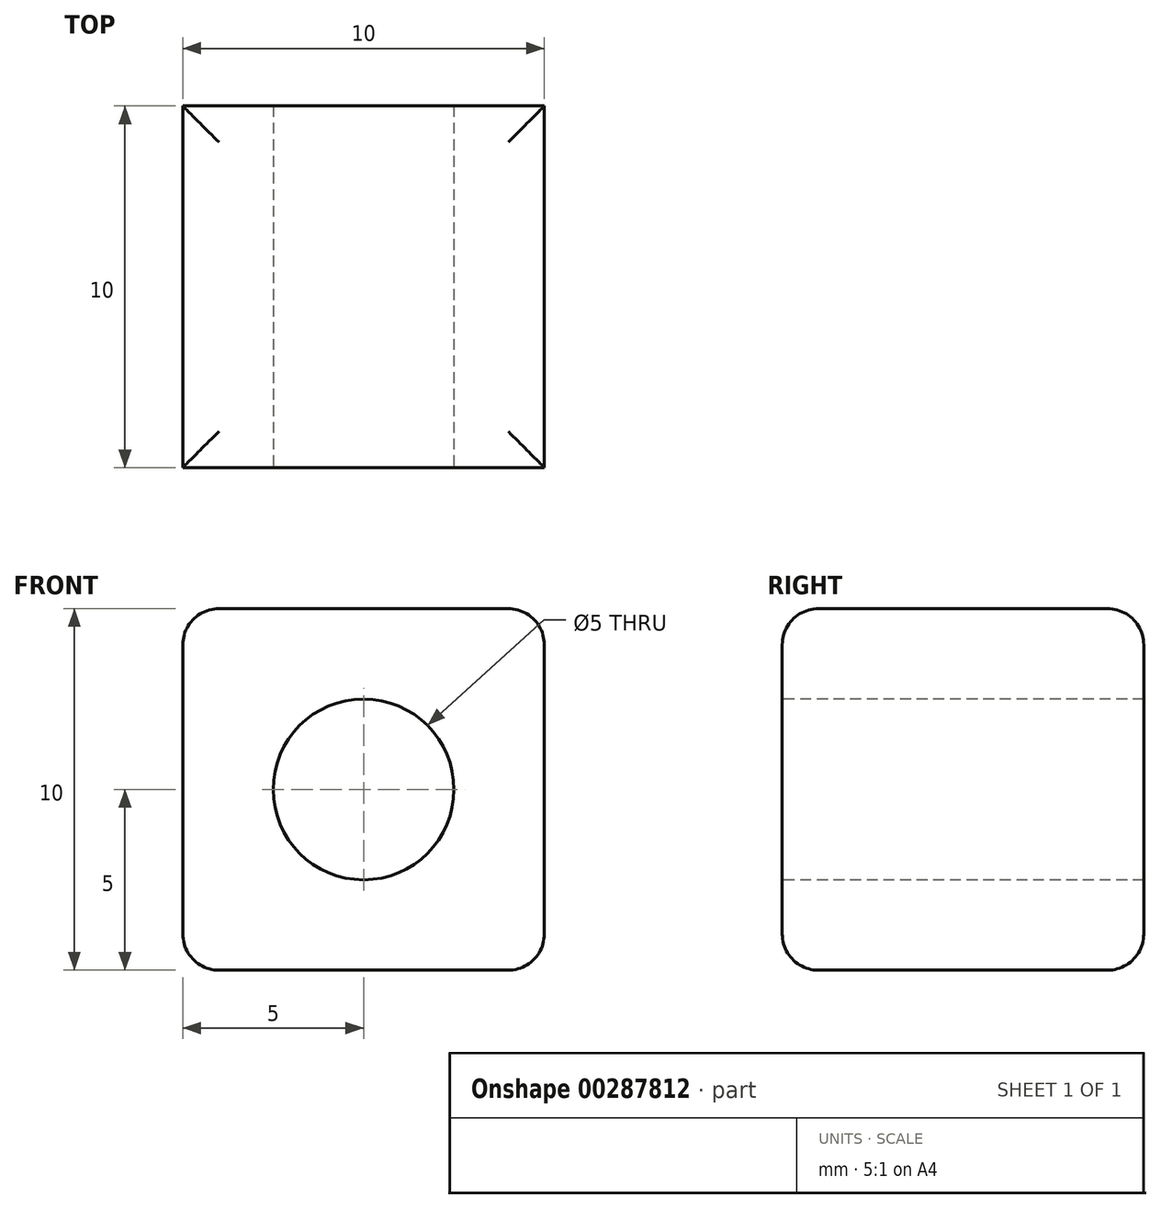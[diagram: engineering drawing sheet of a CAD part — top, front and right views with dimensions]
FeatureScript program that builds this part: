
annotation { "Feature Type Name" : "Feature", "Feature Type Description" : "" }
export const myFeature = defineFeature(function(context is Context, id is Id, definition is map)
    precondition{}
    {
        {
            var Q0;
            Q0=qCreatedBy(makeId("Top.planeOp"),FACE);
            var sketch = newSketch(context, id + "F0", { "sketchPlane" : qUnion([Q0])});
            skLineSegment(sketch, "E0.bottom", {"start": v(5, 5) * mm, "end": v(-5, 5) * mm});
            skLineSegment(sketch, "E0.top", {"start": v(5, -5) * mm, "end": v(-5, -5) * mm});
            skLineSegment(sketch, "E0.left", {"start": v(5, 5) * mm, "end": v(5, -5) * mm});
            skLineSegment(sketch, "E0.right", {"start": v(-5, 5) * mm, "end": v(-5, -5) * mm});
            skPoint(sketch, "E0.middle", {"position": v(0, 0) * mm});
            skSolve(sketch);
        }
        {
            var Q0;
            Q0=makeQuery(id+"F0.imprint","IMPRINT",FACE,{"disambiguationData":[TD([[makeQuery(id+"F0.imprint","IMPRINT",EDGE,{"derivedFrom":sQuery(id+"F0.wireOp",EDGE,"E0.bottom")}),1.0]])]});
            extrude(context, id + "F1", {"entities" : qUnion([Q0]), "depth" : 10 * mm});
        }
        {
            var Q0;
            Q0=makeQuery(id+"F1.opExtrude","SWEPT_FACE",FACE,{"disambiguationData":[OSD([sQuery(id+"F0.wireOp",EDGE,"E0.top")])]});
            var sketch = newSketch(context, id + "F2", { "sketchPlane" : qUnion([Q0])});
            skLineSegment(sketch, "E1", {"start": v(0, 10) * mm, "end": v(0, 0) * mm, "construction": true});
            skLineSegment(sketch, "E2", {"start": v(-5, 5) * mm, "end": v(0, 5) * mm, "construction": true});
            skCircle(sketch, "E3", {"center": v(0, 5) * mm, "radius": 2.5 * mm});
            skSolve(sketch);
        }
        {
            var Q0;
            Q0=makeQuery(id+"F2.imprint","IMPRINT",FACE,{"disambiguationData":[TD([[makeQuery(id+"F2.imprint","IMPRINT",EDGE,{"derivedFrom":sQuery(id+"F2.wireOp",EDGE,"E3")}),1.0]])]});
            extrude(context, id + "F3", {"entities" : qUnion([Q0]), "operationType" : NewBodyOperationType.REMOVE, "oppositeDirection" : true, "depth" : 10.1 * mm});
        }
        {
            var Q0;
            Q0=makeQuery(id+"F1.opExtrude","CAP_EDGE",EDGE,{"disambiguationData":[OSD([sQuery(id+"F0.wireOp",EDGE,"E0.left")])],"isStart":false});
            var Q1;
            Q1=makeQuery(id+"F1.opExtrude","CAP_EDGE",EDGE,{"disambiguationData":[OSD([sQuery(id+"F0.wireOp",EDGE,"E0.bottom")])],"isStart":false});
            var Q2;
            Q2=makeQuery(id+"F1.opExtrude","CAP_EDGE",EDGE,{"disambiguationData":[OSD([sQuery(id+"F0.wireOp",EDGE,"E0.right")])],"isStart":false});
            var Q3;
            Q3=makeQuery(id+"F1.opExtrude","CAP_EDGE",EDGE,{"disambiguationData":[OSD([sQuery(id+"F0.wireOp",EDGE,"E0.top")])],"isStart":false});
            var Q4;
            Q4=makeQuery(id+"F1.opExtrude","CAP_EDGE",EDGE,{"disambiguationData":[OSD([sQuery(id+"F0.wireOp",EDGE,"E0.left")])],"isStart":true});
            var Q5;
            Q5=makeQuery(id+"F1.opExtrude","CAP_EDGE",EDGE,{"disambiguationData":[OSD([sQuery(id+"F0.wireOp",EDGE,"E0.bottom")])],"isStart":true});
            var Q6;
            Q6=makeQuery(id+"F1.opExtrude","CAP_EDGE",EDGE,{"disambiguationData":[OSD([sQuery(id+"F0.wireOp",EDGE,"E0.right")])],"isStart":true});
            var Q7;
            Q7=makeQuery(id+"F1.opExtrude","CAP_EDGE",EDGE,{"disambiguationData":[OSD([sQuery(id+"F0.wireOp",EDGE,"E0.top")])],"isStart":true});
            fillet(context, id + "F4", {"entities" : qUnion([Q0, Q1, Q2, Q3, Q4, Q5, Q6, Q7]), "radius" : 1 * mm, "tangentPropagation" : true, "allowEdgeOverflow" : false});
        }
    });
